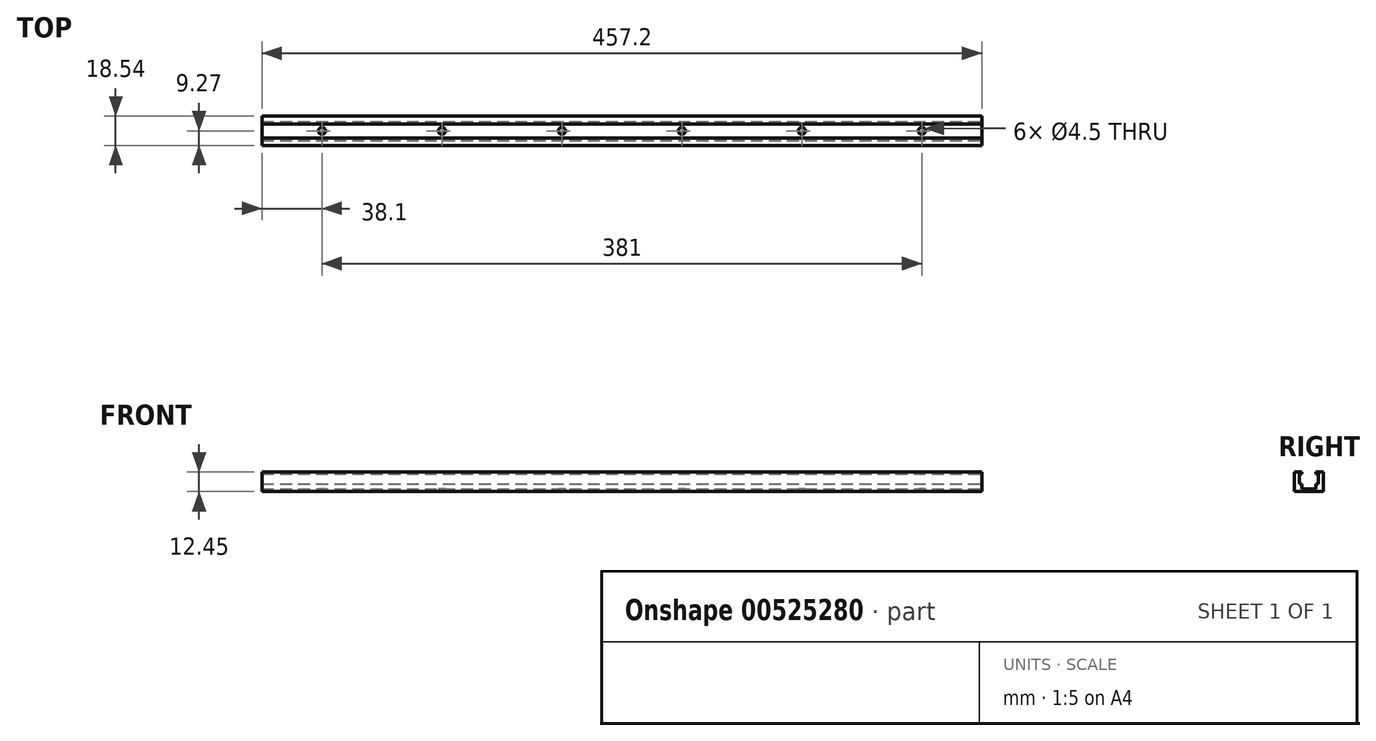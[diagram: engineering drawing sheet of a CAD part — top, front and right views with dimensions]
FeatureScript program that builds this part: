
annotation { "Feature Type Name" : "Feature", "Feature Type Description" : "" }
export const myFeature = defineFeature(function(context is Context, id is Id, definition is map)
    precondition{}
    {
        {
            var Q0;
            Q0=qCreatedBy(makeId("Right.planeOp"),FACE);
            var sketch = newSketch(context, id + "F0", { "sketchPlane" : qUnion([Q0])});
            skLineSegment(sketch, "E0", {"start": v(0, 74.18) * mm, "end": v(0, -81.55) * mm, "construction": true});
            skLineSegment(sketch, "E1", {"start": v(0, 0) * mm, "end": v(9.27, 0) * mm});
            skLineSegment(sketch, "E2", {"start": v(9.27, 0) * mm, "end": v(9.27, 12.45) * mm});
            skLineSegment(sketch, "E3", {"start": v(9.27, 12.45) * mm, "end": v(4.45, 12.45) * mm});
            skLineSegment(sketch, "E4", {"start": v(4.45, 12.45) * mm, "end": v(4.45, 11.18) * mm});
            skLineSegment(sketch, "E5", {"start": v(4.45, 11.18) * mm, "end": v(6.03, 11.18) * mm});
            skLineSegment(sketch, "E6", {"start": v(6.03, 11.18) * mm, "end": v(6.03, 4.95) * mm});
            skLineSegment(sketch, "E7", {"start": v(6.03, 4.95) * mm, "end": v(4.45, 4.95) * mm});
            skLineSegment(sketch, "E8", {"start": v(4.45, 4.95) * mm, "end": v(4.45, 1.78) * mm});
            skLineSegment(sketch, "E9", {"start": v(4.45, 1.78) * mm, "end": v(0, 1.78) * mm});
            skLineSegment(sketch, "E10.MirrorCS", {"start": v(-6.03, 4.95) * mm, "end": v(-4.45, 4.95) * mm});
            skLineSegment(sketch, "E11.MirrorCS", {"start": v(0, 0) * mm, "end": v(-9.27, 0) * mm});
            skLineSegment(sketch, "E12.MirrorCS", {"start": v(-4.45, 1.78) * mm, "end": v(0, 1.78) * mm});
            skLineSegment(sketch, "E13.MirrorCS", {"start": v(-9.27, 0) * mm, "end": v(-9.27, 12.45) * mm});
            skLineSegment(sketch, "E14.MirrorCS", {"start": v(-4.45, 4.95) * mm, "end": v(-4.45, 1.78) * mm});
            skLineSegment(sketch, "E15.MirrorCS", {"start": v(-9.27, 12.45) * mm, "end": v(-4.45, 12.45) * mm});
            skLineSegment(sketch, "E16.MirrorCS", {"start": v(-4.45, 12.45) * mm, "end": v(-4.45, 11.18) * mm});
            skLineSegment(sketch, "E17.MirrorCS", {"start": v(-6.03, 11.18) * mm, "end": v(-6.03, 4.95) * mm});
            skLineSegment(sketch, "E18.MirrorCS", {"start": v(-4.45, 11.18) * mm, "end": v(-6.03, 11.18) * mm});
            skSolve(sketch);
        }
        {
            var Q0;
            Q0 = qSketchRegion(id + "F0", true);
            extrude(context, id + "F1", {"entities" : qUnion([Q0]), "oppositeDirection" : true, "depth" : 457.2 * mm, "offsetDistance" : 25.4 * mm});
        }
        {
            var Q0;
            Q0=makeQuery(id+"F1.opExtrude","SWEPT_FACE",FACE,{"disambiguationData":[OSD([sQuery(id+"F0.wireOp",EDGE,"E1"),sQuery(id+"F0.wireOp",EDGE,"E11.MirrorCS")])]});
            var sketch = newSketch(context, id + "F2", { "sketchPlane" : qUnion([Q0])});
            skPoint(sketch, "E19", {"position": v(-38.1, 0) * mm});
            skPoint(sketch, "E19.positionSnap0", {"position": v(0, 0) * mm});
            skPoint(sketch, "E20.1.0.0", {"position": v(-114.3, 0) * mm});
            skPoint(sketch, "E20.2.0.0", {"position": v(-190.5, 0) * mm});
            skPoint(sketch, "E20.3.0.0", {"position": v(-266.7, 0) * mm});
            skPoint(sketch, "E20.4.0.0", {"position": v(-342.9, 0) * mm});
            skPoint(sketch, "E20.5.0.0", {"position": v(-419.1, 0) * mm});
            skLineSegment(sketch, "E20.direction1", {"start": v(-38.1, 0) * mm, "end": v(-114.3, 0) * mm, "construction": true});
            skSolve(sketch);
        }
        {
            var Q0;
            Q0=sQuery(id+"F2.wireOp",VERTEX,"E19");
            var Q1;
            Q1=sQuery(id+"F2.wireOp",VERTEX,"E20.1.0.0");
            var Q2;
            Q2=sQuery(id+"F2.wireOp",VERTEX,"E20.2.0.0");
            var Q3;
            Q3=sQuery(id+"F2.wireOp",VERTEX,"E20.3.0.0");
            var Q4;
            Q4=sQuery(id+"F2.wireOp",VERTEX,"E20.4.0.0");
            var Q5;
            Q5=sQuery(id+"F2.wireOp",VERTEX,"E20.5.0.0");
            var Q6;
            Q6=makeQuery(id+"F1.opExtrude","SWEPT_BODY",BODY,{"disambiguationData":[OSD([sQuery(id+"F0.wireOp",EDGE,"E1"),sQuery(id+"F0.wireOp",EDGE,"E2"),sQuery(id+"F0.wireOp",EDGE,"E3"),sQuery(id+"F0.wireOp",EDGE,"E4"),sQuery(id+"F0.wireOp",EDGE,"E5"),sQuery(id+"F0.wireOp",EDGE,"E6"),sQuery(id+"F0.wireOp",EDGE,"E7"),sQuery(id+"F0.wireOp",EDGE,"E8"),sQuery(id+"F0.wireOp",EDGE,"E9"),sQuery(id+"F0.wireOp",EDGE,"E10.MirrorCS"),sQuery(id+"F0.wireOp",EDGE,"E11.MirrorCS"),sQuery(id+"F0.wireOp",EDGE,"E12.MirrorCS"),sQuery(id+"F0.wireOp",EDGE,"E13.MirrorCS"),sQuery(id+"F0.wireOp",EDGE,"E14.MirrorCS"),sQuery(id+"F0.wireOp",EDGE,"E15.MirrorCS"),sQuery(id+"F0.wireOp",EDGE,"E16.MirrorCS"),sQuery(id+"F0.wireOp",EDGE,"E17.MirrorCS"),sQuery(id+"F0.wireOp",EDGE,"E18.MirrorCS")])]});
            hole(context, id + "F3", {"style" : HoleStyle.SIMPLE, "endStyle" : HoleEndStyle.THROUGH, "standardTappedOrClearance" : lookupTablePath({ "standard" : "ANSI", "fit" : "Normal (ASME)", "size" : "#8", "type" : "Clearance" }), "standardBlindInLast" : lookupTablePath({ "fit" : "Free", "standard" : "ANSI", "size" : "#8", "type" : "Clearance" }), "holeDiameter" : 4.5 * mm, "isTappedThrough" : true, "tappedDepth" : 12.7 * mm, "tapClearance" : 3, "locations" : qUnion([Q0, Q1, Q2, Q3, Q4, Q5]), "scope" : qUnion([Q6])});
        }
    });
